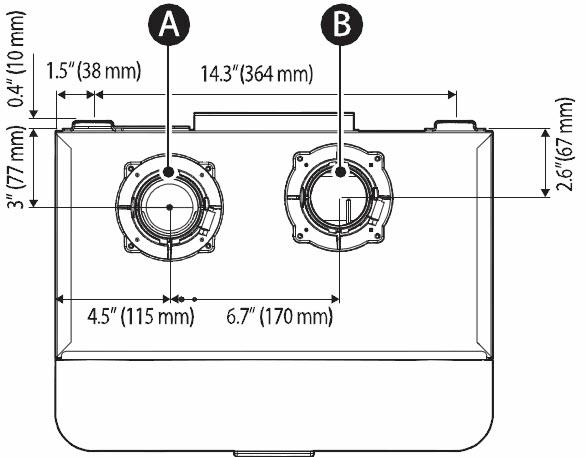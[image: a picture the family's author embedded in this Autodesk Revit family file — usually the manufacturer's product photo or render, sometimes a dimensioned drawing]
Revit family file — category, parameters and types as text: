
# Revit family: Water_Heater-Racks-Navien-NPE-14_Unit_Front---
name_source: partatom
category: Mechanical Equipment
revit_build: Autodesk Revit 2016 (Build: 20150220_1215(x64)
units: mm (PartAtom-declared; Revit-internal decimal feet)

## family parameters
Cut with Voids When Loaded = No
Host = Face
OmniClass Number = 23.65.35.11
OmniClass Title = Supply Water Heaters
Part Type = Normal
Room Calculation Point = No
Round Connector Dimension = Use Diameter
Shared = No

## types (4) — shared parameters
2" Exhaust/Intake = Yes
3" Exhaust/Intake = No
Apparent Load = 0 VA
Assembly Code = D3010500
Certifications = Energy Star | AHRI | CSA | CSA | NFS
Cold Water Inlet = 1"
Configuration = NPE_F14_4F3F_4F3F
Default Elevation = 48 "
Depth = 23.8 "
Description = 14 Unit Front
Exhaust = 2"
Finish = Metal - Navien - White
Flow Rate = 1 GPM
Flow Rate Note = 35°F (19°C) temp rise: 11.2 GPM (42 L/m) | 45°F (25°C) temp rise: 8.7 GPM (33 L/m) | 67°F (36°C) temp rise: NPE-240A: 5.6 GPM(21 L/m), NPE-240S: 5.7 GPM(22 L/m)
Frequency = 60 Hz
Gas Inlet = 1"
Heating Capacity = 120000.0 Btu/h
Heating Capacity Note = 19,900–199,900 (BTU/H)
Height = 65.5 "
Hot Water Outlet = 1"
Ignition = Electronic ignition
Installation Type = Indoor
Intake = 2"
Keynote = 22 33 00.A1
Manifold(s) = (2) 30019041A + (2) 30019043A
Manufacturer = Navien, Inc.
Manufacturer Fax Number = (949) 420-0430
Natural Gas Manifold Pressure = -0.05" WC to -0.58" WC
Natural Gas Supply Pressure = 3.5"–10.5" WC
Number of Poles = 1
Phase = 1
Power Factor = 1
Product Documentation Link = https://www.navieninc.com
Product Name = NPE Series Tankless Water Heaters w/ Racks
Product Page URL = https://www.navieninc.com
Propane Gas Manifold Pressure = -0.10" WC to -0.78" WC
Propane Gas Supply Pressure = 8"–13" WC
Rack(s) = (2) GFFM-KDIZUS-003 + (12) GFFM-KDIZUS-004
Required Cascade Operation Accessory = (14) 30014367A (Common Vent Damper & Cascade Communication Cable) or (13) GXXX000546 (Individual Vent Cascade Communication Cable)
Type Comments = For Wall Mount RL Manifold systems- Exclude Base & Add-on Racks
URL = https://www.navieninc.com
Venting = Exhaust: 2" PVC, CPVC, PP, SS / 2" special gas vent type BH (Class II, A/B/C) | Intake: 2" PVC, CPVC, PP, SS / 2" special gas vent type BH (Class II, A/B/C) | Vent clearances: 0" to combustibles
Venting Type = Forced draft direct vent
Version = 2016 - v1.0.a
Voltage = 120 V
Water Pressure = 15–150 PSI
Wi-Fi Ready = NaviLink Wi-Fi Control: PBCM-AS-001
Width = 302.3 "

## per-type parameters (varying)
| type | Constraints | Model | Natural Gas | Propane Gas | Recirculation Inlet | Recirculation Inlet Visibility | Tankless Water Heaters | Weight |
| Natural Gas - Recirculating System - NPE-240A(Advanced)-NG | 6 | (14) NPE-240A-NG | Yes | No | 0" | Yes | (14) NPE-240A-NG | 82.00 lbf |
| Natural Gas - NPE-240S(Standard)-NG | 7 | (14) NPE-240S-NG | Yes | No | 1" | No | (14) NPE-240S-NG | 75.00 lbf |
| Propane Gas - Recirculating System - NPE-240A(Advanced)-LPG | 6 | (14) NPE-240A-LPG | No | Yes | 0" | Yes | (14) NPE-240A-LPG | 82.00 lbf |
| Propane Gas - NPE-240S(Standard)-LPG | 7 | (14) NPE-240S-LPG | No | Yes | 1" | No | (14) NPE-240S-LPG | 75.00 lbf |

## geometry (parser evidence)
native form markers: Sweep x23
no freeform markers — native parametric forms only
